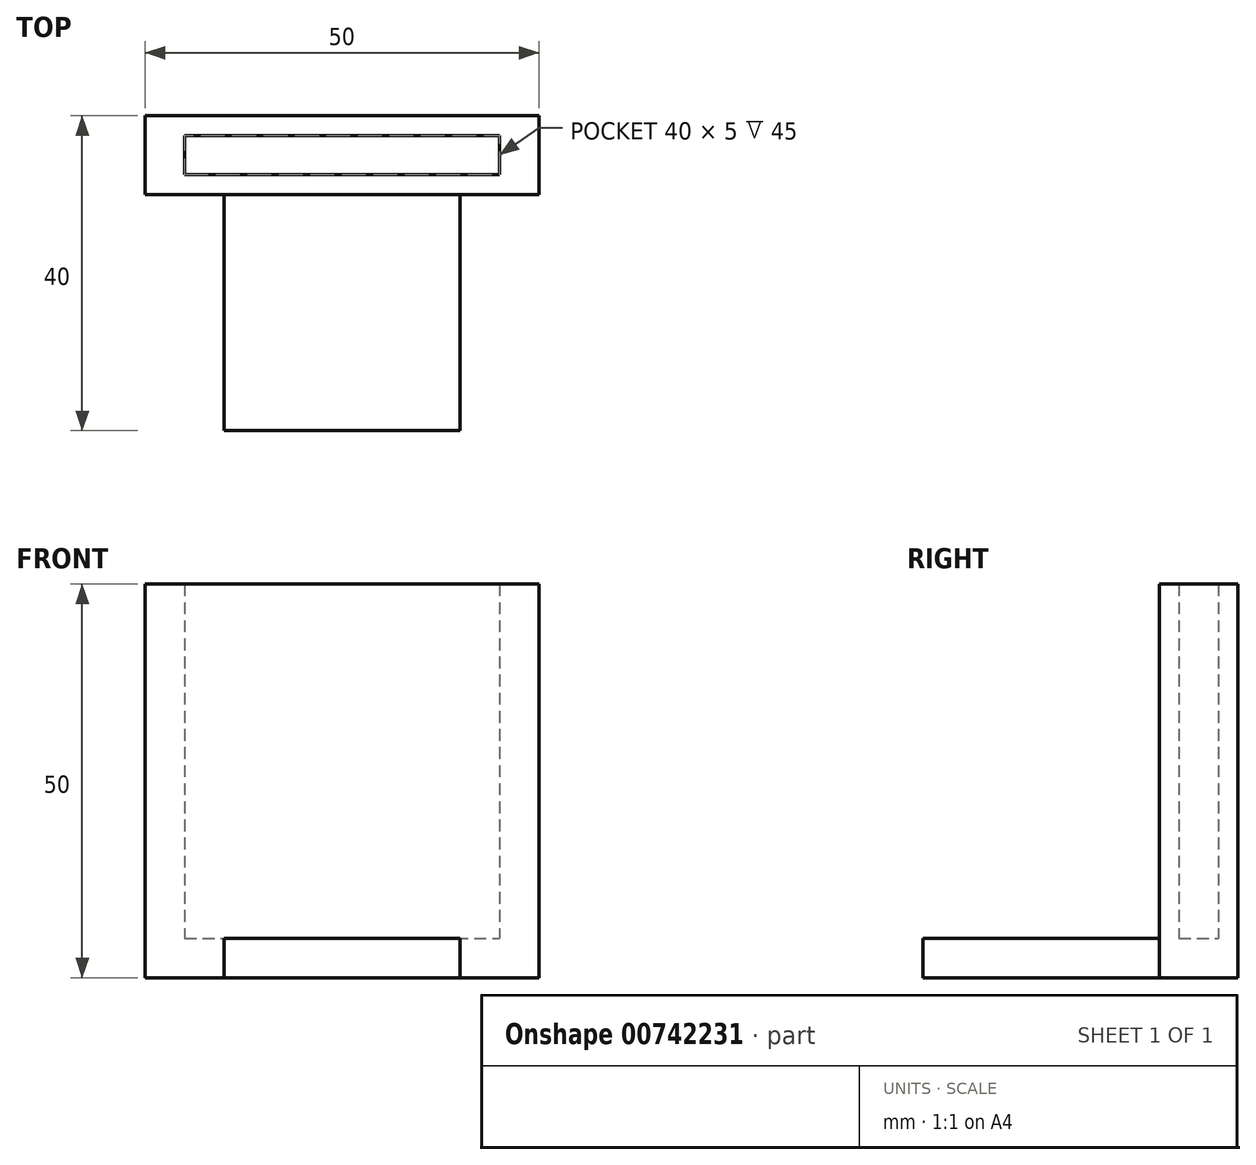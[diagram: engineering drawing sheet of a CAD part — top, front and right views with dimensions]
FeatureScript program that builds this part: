
annotation { "Feature Type Name" : "Feature", "Feature Type Description" : "" }
export const myFeature = defineFeature(function(context is Context, id is Id, definition is map)
    precondition{}
    {
        {
            var Q0;
            Q0=qCreatedBy(makeId("Top.planeOp"),FACE);
            var sketch = newSketch(context, id + "F0", { "sketchPlane" : qUnion([Q0])});
            skLineSegment(sketch, "E0.bottom", {"start": v(-25, 10) * mm, "end": v(25, 10) * mm});
            skLineSegment(sketch, "E0.top", {"start": v(-25, 0) * mm, "end": v(25, 0) * mm});
            skLineSegment(sketch, "E0.left", {"start": v(-25, 10) * mm, "end": v(-25, 0) * mm});
            skLineSegment(sketch, "E0.right", {"start": v(25, 10) * mm, "end": v(25, 0) * mm});
            skLineSegment(sketch, "E1.bottom", {"start": v(-20, 2.5) * mm, "end": v(20, 2.5) * mm});
            skLineSegment(sketch, "E1.top", {"start": v(-20, 7.5) * mm, "end": v(20, 7.5) * mm});
            skLineSegment(sketch, "E1.left", {"start": v(-20, 2.5) * mm, "end": v(-20, 7.5) * mm});
            skLineSegment(sketch, "E1.right", {"start": v(20, 2.5) * mm, "end": v(20, 7.5) * mm});
            skLineSegment(sketch, "E2.bottom", {"start": v(-15, 0) * mm, "end": v(15, 0) * mm});
            skLineSegment(sketch, "E2.top", {"start": v(-15, -30) * mm, "end": v(15, -30) * mm});
            skLineSegment(sketch, "E2.left", {"start": v(-15, 0) * mm, "end": v(-15, -30) * mm});
            skLineSegment(sketch, "E2.right", {"start": v(15, 0) * mm, "end": v(15, -30) * mm});
            skSolve(sketch);
        }
        {
            var Q0;
            Q0=makeQuery(id+"F0.imprint","IMPRINT",FACE,{"disambiguationData":[TD([[makeQuery(id+"F0.imprint","IMPRINT",EDGE,{"derivedFrom":sQuery(id+"F0.wireOp",EDGE,"E0.bottom")}),-1.0]])]});
            extrude(context, id + "F1", {"entities" : qUnion([Q0]), "depth" : 50 * mm, "offsetDistance" : 25 * mm});
        }
        {
            var Q0;
            Q0=makeQuery(id+"F0.imprint","IMPRINT",FACE,{"disambiguationData":[TD([[makeQuery(id+"F0.imprint","IMPRINT",EDGE,{"derivedFrom":sQuery(id+"F0.wireOp",EDGE,"E2.top")}),1.0]])]});
            var Q1;
            Q1=makeQuery(id+"F0.imprint","IMPRINT",FACE,{"disambiguationData":[TD([[makeQuery(id+"F0.imprint","IMPRINT",EDGE,{"derivedFrom":sQuery(id+"F0.wireOp",EDGE,"E1.bottom")}),1.0]])]});
            extrude(context, id + "F2", {"entities" : qUnion([Q0, Q1]), "operationType" : NewBodyOperationType.ADD, "depth" : 5 * mm, "offsetDistance" : 25 * mm});
        }
    });
